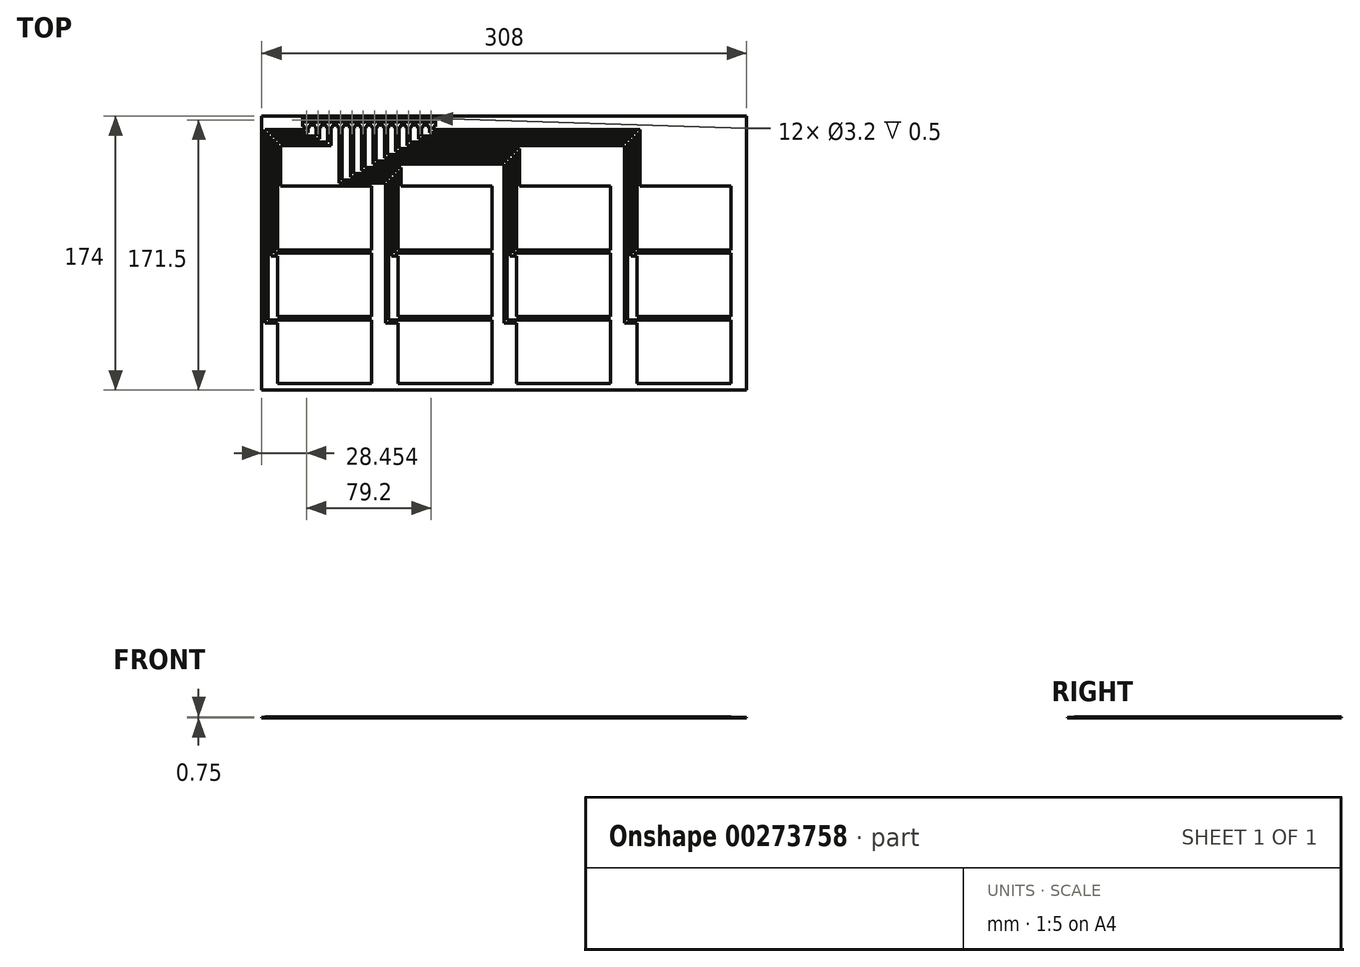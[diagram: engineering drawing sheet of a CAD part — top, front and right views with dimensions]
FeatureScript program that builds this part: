
annotation { "Feature Type Name" : "Feature", "Feature Type Description" : "" }
export const myFeature = defineFeature(function(context is Context, id is Id, definition is map)
    precondition{}
    {
        {
            var Q0;
            Q0=qCreatedBy(makeId("Top.planeOp"),FACE);
            var sketch = newSketch(context, id + "F0", { "sketchPlane" : qUnion([Q0])});
            skLineSegment(sketch, "E0.bottom", {"start": v(154, 87) * mm, "end": v(-154, 87) * mm});
            skLineSegment(sketch, "E0.top", {"start": v(154, -87) * mm, "end": v(-154, -87) * mm});
            skLineSegment(sketch, "E0.left", {"start": v(154, 87) * mm, "end": v(154, -87) * mm});
            skLineSegment(sketch, "E0.right", {"start": v(-154, 87) * mm, "end": v(-154, -87) * mm});
            skPoint(sketch, "E0.middle", {"position": v(0, 0) * mm});
            skSolve(sketch);
        }
        {
            var Q0;
            Q0=makeQuery(id+"F0.imprint","IMPRINT",FACE,{"disambiguationData":[TD([[makeQuery(id+"F0.imprint","IMPRINT",EDGE,{"derivedFrom":sQuery(id+"F0.wireOp",EDGE,"E0.bottom")}),1.0]])]});
            extrude(context, id + "F1", {"entities" : qUnion([Q0]), "depth" : .25 * mm});
        }
        {
            var Q0;
            Q0=makeQuery(id+"F1.opExtrude","CAP_FACE",FACE,{"disambiguationData":[OSD([sQuery(id+"F0.wireOp",EDGE,"E0.bottom"),sQuery(id+"F0.wireOp",EDGE,"E0.top"),sQuery(id+"F0.wireOp",EDGE,"E0.left"),sQuery(id+"F0.wireOp",EDGE,"E0.right")])],"isStart":false});
            var sketch = newSketch(context, id + "F2", { "sketchPlane" : qUnion([Q0])});
            skLineSegment(sketch, "E1", {"start": v(-85.95, 87) * mm, "end": v(-85.95, 80.4) * mm, "construction": true});
            skCircle(sketch, "E2", {"center": v(-89.55, 84.5) * mm, "radius": 1.6 * mm});
            skLineSegment(sketch, "E3", {"start": v(-89.55, 84.5) * mm, "end": v(-89.55, 80.4) * mm, "construction": true});
            skPoint(sketch, "E4", {"position": v(0, 80.62) * mm});
            skLineSegment(sketch, "E5.direction1", {"start": v(-89.55, 84.5) * mm, "end": v(-82.35, 84.5) * mm, "construction": true});
            skLineSegment(sketch, "E6", {"start": v(-86.95, 87) * mm, "end": v(-86.95, 80.4) * mm});
            skLineSegment(sketch, "E7.MirrorCS", {"start": v(-92.15, 87) * mm, "end": v(-92.15, 80.4) * mm});
            skLineSegment(sketch, "E8.trimOffspring", {"start": v(-92.15, 80.4) * mm, "end": v(-86.95, 80.4) * mm});
            skLineSegment(sketch, "E9.trimOffspring", {"start": v(-92.15, 87) * mm, "end": v(-86.95, 87) * mm});
            skCircle(sketch, "E10.1.0.0", {"center": v(-96.75, 84.5) * mm, "radius": 1.6 * mm});
            skLineSegment(sketch, "E10.1.0.1", {"start": v(-99.35, 87) * mm, "end": v(-99.35, 80.4) * mm});
            skLineSegment(sketch, "E10.1.0.2", {"start": v(-99.35, 87) * mm, "end": v(-94.15, 87) * mm});
            skLineSegment(sketch, "E10.1.0.3", {"start": v(-94.15, 87) * mm, "end": v(-94.15, 80.4) * mm});
            skLineSegment(sketch, "E10.1.0.4", {"start": v(-99.35, 80.4) * mm, "end": v(-94.15, 80.4) * mm});
            skCircle(sketch, "E10.2.0.0", {"center": v(-103.95, 84.5) * mm, "radius": 1.6 * mm});
            skLineSegment(sketch, "E10.2.0.1", {"start": v(-106.55, 87) * mm, "end": v(-106.55, 80.4) * mm});
            skLineSegment(sketch, "E10.2.0.2", {"start": v(-106.55, 87) * mm, "end": v(-101.35, 87) * mm});
            skLineSegment(sketch, "E10.2.0.3", {"start": v(-101.35, 87) * mm, "end": v(-101.35, 80.4) * mm});
            skLineSegment(sketch, "E10.2.0.4", {"start": v(-106.55, 80.4) * mm, "end": v(-101.35, 80.4) * mm});
            skCircle(sketch, "E10.3.0.0", {"center": v(-111.15, 84.5) * mm, "radius": 1.6 * mm});
            skLineSegment(sketch, "E10.3.0.1", {"start": v(-113.75, 87) * mm, "end": v(-113.75, 80.4) * mm});
            skLineSegment(sketch, "E10.3.0.2", {"start": v(-113.75, 87) * mm, "end": v(-108.55, 87) * mm});
            skLineSegment(sketch, "E10.3.0.3", {"start": v(-108.55, 87) * mm, "end": v(-108.55, 80.4) * mm});
            skLineSegment(sketch, "E10.3.0.4", {"start": v(-113.75, 80.4) * mm, "end": v(-108.55, 80.4) * mm});
            skCircle(sketch, "E10.4.0.0", {"center": v(-118.35, 84.5) * mm, "radius": 1.6 * mm});
            skLineSegment(sketch, "E10.4.0.1", {"start": v(-120.95, 87) * mm, "end": v(-120.95, 80.4) * mm});
            skLineSegment(sketch, "E10.4.0.2", {"start": v(-120.95, 87) * mm, "end": v(-115.75, 87) * mm});
            skLineSegment(sketch, "E10.4.0.3", {"start": v(-115.75, 87) * mm, "end": v(-115.75, 80.4) * mm});
            skLineSegment(sketch, "E10.4.0.4", {"start": v(-120.95, 80.4) * mm, "end": v(-115.75, 80.4) * mm});
            skCircle(sketch, "E10.5.0.0", {"center": v(-125.55, 84.5) * mm, "radius": 1.6 * mm});
            skLineSegment(sketch, "E10.5.0.1", {"start": v(-128.15, 87) * mm, "end": v(-128.15, 80.4) * mm});
            skLineSegment(sketch, "E10.5.0.2", {"start": v(-128.15, 87) * mm, "end": v(-122.95, 87) * mm});
            skLineSegment(sketch, "E10.5.0.3", {"start": v(-122.95, 87) * mm, "end": v(-122.95, 80.4) * mm});
            skLineSegment(sketch, "E10.5.0.4", {"start": v(-128.15, 80.4) * mm, "end": v(-122.95, 80.4) * mm});
            skLineSegment(sketch, "E10.direction1", {"start": v(-89.55, 84.5) * mm, "end": v(-96.75, 84.5) * mm, "construction": true});
            skCircle(sketch, "E11.MirrorC", {"center": v(-82.35, 84.5) * mm, "radius": 1.6 * mm});
            skLineSegment(sketch, "E12.MirrorCS", {"start": v(-79.75, 80.4) * mm, "end": v(-84.95, 80.4) * mm});
            skLineSegment(sketch, "E13.MirrorCS", {"start": v(-84.95, 87) * mm, "end": v(-84.95, 80.4) * mm});
            skLineSegment(sketch, "E14.MirrorCS", {"start": v(-79.75, 87) * mm, "end": v(-84.95, 87) * mm});
            skLineSegment(sketch, "E15.MirrorCS", {"start": v(-79.75, 87) * mm, "end": v(-79.75, 80.4) * mm});
            skLineSegment(sketch, "E16.MirrorCS", {"start": v(-77.75, 87) * mm, "end": v(-77.75, 80.4) * mm});
            skCircle(sketch, "E17.MirrorC", {"center": v(-75.15, 84.5) * mm, "radius": 1.6 * mm});
            skLineSegment(sketch, "E18.MirrorCS", {"start": v(-72.55, 87) * mm, "end": v(-77.75, 87) * mm});
            skLineSegment(sketch, "E19.MirrorCS", {"start": v(-72.55, 87) * mm, "end": v(-72.55, 80.4) * mm});
            skLineSegment(sketch, "E20.MirrorCS", {"start": v(-70.55, 87) * mm, "end": v(-70.55, 80.4) * mm});
            skCircle(sketch, "E21.MirrorC", {"center": v(-67.95, 84.5) * mm, "radius": 1.6 * mm});
            skLineSegment(sketch, "E22.MirrorCS", {"start": v(-65.35, 87) * mm, "end": v(-65.35, 80.4) * mm});
            skLineSegment(sketch, "E23.MirrorCS", {"start": v(-65.35, 87) * mm, "end": v(-70.55, 87) * mm});
            skLineSegment(sketch, "E24.MirrorCS", {"start": v(-63.35, 87) * mm, "end": v(-63.35, 80.4) * mm});
            skLineSegment(sketch, "E25.MirrorCS", {"start": v(-58.15, 87) * mm, "end": v(-63.35, 87) * mm});
            skCircle(sketch, "E26.MirrorC", {"center": v(-60.75, 84.5) * mm, "radius": 1.6 * mm});
            skLineSegment(sketch, "E27.MirrorCS", {"start": v(-58.15, 87) * mm, "end": v(-58.15, 80.4) * mm});
            skLineSegment(sketch, "E28.MirrorCS", {"start": v(-58.15, 80.4) * mm, "end": v(-63.35, 80.4) * mm});
            skLineSegment(sketch, "E29.MirrorCS", {"start": v(-56.15, 87) * mm, "end": v(-56.15, 80.4) * mm});
            skLineSegment(sketch, "E30.MirrorCS", {"start": v(-50.95, 87) * mm, "end": v(-56.15, 87) * mm});
            skLineSegment(sketch, "E31.MirrorCS", {"start": v(-50.95, 87) * mm, "end": v(-50.95, 80.4) * mm});
            skCircle(sketch, "E32.MirrorC", {"center": v(-53.55, 84.5) * mm, "radius": 1.6 * mm});
            skLineSegment(sketch, "E33.MirrorCS", {"start": v(-48.95, 87) * mm, "end": v(-48.95, 80.4) * mm});
            skCircle(sketch, "E34.MirrorC", {"center": v(-46.35, 84.5) * mm, "radius": 1.6 * mm});
            skLineSegment(sketch, "E35.MirrorCS", {"start": v(-43.75, 87) * mm, "end": v(-48.95, 87) * mm});
            skLineSegment(sketch, "E36.MirrorCS", {"start": v(-43.75, 87) * mm, "end": v(-43.75, 80.4) * mm});
            skLineSegment(sketch, "E37.top", {"start": v(-84.36, 0) * mm, "end": v(-144, 0) * mm});
            skLineSegment(sketch, "E37.left", {"start": v(-84.36, 42.4) * mm, "end": v(-84.36, 2) * mm});
            skLineSegment(sketch, "E38", {"start": v(0, 87) * mm, "end": v(0, -87) * mm, "construction": true});
            skLineSegment(sketch, "E39.bottom", {"start": v(-67.44, 42.4) * mm, "end": v(-7.8, 42.4) * mm});
            skLineSegment(sketch, "E39.top", {"start": v(-67.44, 2) * mm, "end": v(-7.8, 2) * mm});
            skLineSegment(sketch, "E39.left", {"start": v(-67.44, 42.4) * mm, "end": v(-67.44, 2) * mm});
            skLineSegment(sketch, "E39.right", {"start": v(-7.8, 42.4) * mm, "end": v(-7.8, 2) * mm});
            skLineSegment(sketch, "E40.bottom", {"start": v(-144, 2) * mm, "end": v(-84.36, 2) * mm});
            skLineSegment(sketch, "E40.left", {"start": v(-144, 0) * mm, "end": v(-144, -40.4) * mm});
            skLineSegment(sketch, "E41.left", {"start": v(-144, -42.4) * mm, "end": v(-144, -82.8) * mm});
            skLineSegment(sketch, "E41.right", {"start": v(-84.36, -42.4) * mm, "end": v(-84.36, -82.8) * mm});
            skLineSegment(sketch, "E42.bottom", {"start": v(-67.44, 0) * mm, "end": v(-7.8, 0) * mm});
            skLineSegment(sketch, "E42.top", {"start": v(-67.44, -40.4) * mm, "end": v(-7.8, -40.4) * mm});
            skLineSegment(sketch, "E42.left", {"start": v(-67.44, 0) * mm, "end": v(-67.44, -40.4) * mm});
            skLineSegment(sketch, "E42.right", {"start": v(-7.8, 0) * mm, "end": v(-7.8, -40.4) * mm});
            skLineSegment(sketch, "E43.bottom", {"start": v(-67.44, -42.4) * mm, "end": v(-7.8, -42.4) * mm});
            skLineSegment(sketch, "E43.top", {"start": v(-67.44, -82.8) * mm, "end": v(-7.8, -82.8) * mm});
            skLineSegment(sketch, "E43.left", {"start": v(-67.44, -42.4) * mm, "end": v(-67.44, -82.8) * mm});
            skLineSegment(sketch, "E43.right", {"start": v(-7.8, -42.4) * mm, "end": v(-7.8, -82.8) * mm});
            skLineSegment(sketch, "E44", {"start": v(-144, 87) * mm, "end": v(-154, 87) * mm, "construction": true});
            skLineSegment(sketch, "E45", {"start": v(-36.86, -77) * mm, "end": v(-36.86, -87) * mm, "construction": true});
            skLineSegment(sketch, "E46", {"start": v(-144, -40.4) * mm, "end": v(-144, -42.4) * mm, "construction": true});
            skLineSegment(sketch, "E47", {"start": v(-67.44, 2) * mm, "end": v(-67.44, 0) * mm, "construction": true});
            skLineSegment(sketch, "E48", {"start": v(-67.44, -40.4) * mm, "end": v(-67.44, -42.4) * mm, "construction": true});
            skLineSegment(sketch, "E49", {"start": v(-84.36, 0) * mm, "end": v(-84.36, -40.4) * mm});
            skLineSegment(sketch, "E50", {"start": v(-84.36, -40.4) * mm, "end": v(-144, -40.4) * mm});
            skLineSegment(sketch, "E51", {"start": v(-144, -42.4) * mm, "end": v(-84.36, -42.4) * mm});
            skLineSegment(sketch, "E52", {"start": v(-84.36, 42.4) * mm, "end": v(-67.44, 42.4) * mm, "construction": true});
            skLineSegment(sketch, "E53", {"start": v(-124.55, 80.4) * mm, "end": v(-124.55, 76.4) * mm});
            skLineSegment(sketch, "E54", {"start": v(-124.55, 76.4) * mm, "end": v(-150, 76.4) * mm});
            skLineSegment(sketch, "E55", {"start": v(-150, 76.4) * mm, "end": v(-150, -42.4) * mm});
            skPoint(sketch, "E56", {"position": v(-125.55, 80.4) * mm});
            skPoint(sketch, "E57", {"position": v(-118.35, 80.4) * mm});
            skPoint(sketch, "E58", {"position": v(-111.15, 80.4) * mm});
            skLineSegment(sketch, "E59", {"start": v(-117.35, 80.4) * mm, "end": v(-117.35, 72.4) * mm});
            skLineSegment(sketch, "E60", {"start": v(-117.35, 72.4) * mm, "end": v(-146, 72.4) * mm});
            skLineSegment(sketch, "E61", {"start": v(-146, 72.4) * mm, "end": v(-146, 0) * mm});
            skLineSegment(sketch, "E62", {"start": v(-110.15, 80.4) * mm, "end": v(-110.15, 68.4) * mm});
            skLineSegment(sketch, "E63", {"start": v(-146, 0) * mm, "end": v(-144, 0) * mm});
            skLineSegment(sketch, "E64", {"start": v(-144, -42.4) * mm, "end": v(-150, -42.4) * mm});
            skLineSegment(sketch, "E65.0", {"start": v(-148, -2) * mm, "end": v(-144, -2) * mm});
            skLineSegment(sketch, "E65.1", {"start": v(-148, 74.4) * mm, "end": v(-148, -2) * mm});
            skLineSegment(sketch, "E65.2", {"start": v(-119.35, 74.4) * mm, "end": v(-148, 74.4) * mm});
            skLineSegment(sketch, "E65.3", {"start": v(-119.35, 80.4) * mm, "end": v(-119.35, 74.4) * mm});
            skLineSegment(sketch, "E66.0", {"start": v(-144, -44.4) * mm, "end": v(-152, -44.4) * mm});
            skLineSegment(sketch, "E66.1", {"start": v(-152, 78.4) * mm, "end": v(-152, -44.4) * mm});
            skLineSegment(sketch, "E66.2", {"start": v(-126.55, 78.4) * mm, "end": v(-152, 78.4) * mm});
            skLineSegment(sketch, "E66.3", {"start": v(-126.55, 80.4) * mm, "end": v(-126.55, 78.4) * mm});
            skPoint(sketch, "E67", {"position": v(-103.95, 80.4) * mm});
            skPoint(sketch, "E68", {"position": v(-96.75, 80.4) * mm});
            skPoint(sketch, "E69", {"position": v(-82.35, 80.4) * mm});
            skPoint(sketch, "E70", {"position": v(-75.15, 80.4) * mm});
            skLineSegment(sketch, "E71", {"start": v(-102.95, 80.4) * mm, "end": v(-102.95, 46.4) * mm});
            skLineSegment(sketch, "E72", {"start": v(-102.95, 46.4) * mm, "end": v(-73.44, 46.4) * mm});
            skLineSegment(sketch, "E73", {"start": v(-73.44, 46.4) * mm, "end": v(-73.44, -42.4) * mm});
            skLineSegment(sketch, "E74", {"start": v(-73.44, -42.4) * mm, "end": v(-67.44, -42.4) * mm});
            skLineSegment(sketch, "E75", {"start": v(-95.75, 80.4) * mm, "end": v(-95.75, 50.4) * mm});
            skLineSegment(sketch, "E76", {"start": v(-95.75, 50.4) * mm, "end": v(-69.44, 50.4) * mm});
            skLineSegment(sketch, "E77", {"start": v(-69.44, 50.4) * mm, "end": v(-69.44, 0) * mm});
            skLineSegment(sketch, "E78", {"start": v(-69.44, 0) * mm, "end": v(-67.44, 0) * mm});
            skLineSegment(sketch, "E79.0", {"start": v(-75.44, -44.4) * mm, "end": v(-67.44, -44.4) * mm});
            skLineSegment(sketch, "E79.1", {"start": v(-75.44, 44.4) * mm, "end": v(-75.44, -44.4) * mm});
            skLineSegment(sketch, "E79.2", {"start": v(-104.95, 44.4) * mm, "end": v(-75.44, 44.4) * mm});
            skLineSegment(sketch, "E79.3", {"start": v(-104.95, 80.4) * mm, "end": v(-104.95, 44.4) * mm});
            skLineSegment(sketch, "E80.0", {"start": v(-71.44, -2) * mm, "end": v(-67.44, -2) * mm});
            skLineSegment(sketch, "E80.1", {"start": v(-71.44, 48.4) * mm, "end": v(-71.44, -2) * mm});
            skLineSegment(sketch, "E80.2", {"start": v(-97.75, 48.4) * mm, "end": v(-71.44, 48.4) * mm});
            skLineSegment(sketch, "E80.3", {"start": v(-97.75, 80.4) * mm, "end": v(-97.75, 48.4) * mm});
            skLineSegment(sketch, "E81", {"start": v(-84.36, -42.4) * mm, "end": v(-73.44, -42.4) * mm, "construction": true});
            skLineSegment(sketch, "E82", {"start": v(-84.36, 0) * mm, "end": v(-69.44, 0) * mm, "construction": true});
            skLineSegment(sketch, "E83", {"start": v(-88.55, 80.4) * mm, "end": v(-88.55, 54.4) * mm});
            skLineSegment(sketch, "E84", {"start": v(-88.55, 54.4) * mm, "end": v(-65.44, 54.4) * mm});
            skLineSegment(sketch, "E85", {"start": v(-65.44, 54.4) * mm, "end": v(-65.44, 42.4) * mm});
            skLineSegment(sketch, "E86", {"start": v(-81.35, 80.4) * mm, "end": v(-81.35, 58.4) * mm});
            skLineSegment(sketch, "E87", {"start": v(-144, 42.4) * mm, "end": v(-144, 2) * mm});
            skLineSegment(sketch, "E88", {"start": v(-144, 2) * mm, "end": v(-144, 0) * mm, "construction": true});
            skLineSegment(sketch, "E89.MirrorCS", {"start": v(7.8, 42.4) * mm, "end": v(7.8, 2) * mm});
            skLineSegment(sketch, "E90.MirrorCS", {"start": v(67.44, 42.4) * mm, "end": v(7.8, 42.4) * mm});
            skLineSegment(sketch, "E91.MirrorCS", {"start": v(67.44, 42.4) * mm, "end": v(67.44, 2) * mm});
            skLineSegment(sketch, "E92.MirrorCS", {"start": v(67.44, 2) * mm, "end": v(7.8, 2) * mm});
            skLineSegment(sketch, "E93.MirrorCS", {"start": v(84.36, 42.4) * mm, "end": v(84.36, 2) * mm});
            skLineSegment(sketch, "E94.MirrorCS", {"start": v(84.36, 42.4) * mm, "end": v(144, 42.4) * mm});
            skLineSegment(sketch, "E95.MirrorCS", {"start": v(144, 42.4) * mm, "end": v(144, 2) * mm});
            skLineSegment(sketch, "E96.MirrorCS", {"start": v(144, 2) * mm, "end": v(84.36, 2) * mm});
            skLineSegment(sketch, "E97.MirrorCS", {"start": v(84.36, 0) * mm, "end": v(144, 0) * mm});
            skLineSegment(sketch, "E98.MirrorCS", {"start": v(144, 0) * mm, "end": v(144, -40.4) * mm});
            skLineSegment(sketch, "E99.MirrorCS", {"start": v(84.36, 0) * mm, "end": v(84.36, -40.4) * mm});
            skLineSegment(sketch, "E100.MirrorCS", {"start": v(144, -42.4) * mm, "end": v(84.36, -42.4) * mm});
            skLineSegment(sketch, "E101.MirrorCS", {"start": v(84.36, -42.4) * mm, "end": v(84.36, -82.8) * mm});
            skLineSegment(sketch, "E102.MirrorCS", {"start": v(67.44, -42.4) * mm, "end": v(67.44, -82.8) * mm});
            skLineSegment(sketch, "E103.MirrorCS", {"start": v(7.8, -42.4) * mm, "end": v(7.8, -82.8) * mm});
            skLineSegment(sketch, "E104.MirrorCS", {"start": v(67.44, -42.4) * mm, "end": v(7.8, -42.4) * mm});
            skLineSegment(sketch, "E105.MirrorCS", {"start": v(67.44, -40.4) * mm, "end": v(7.8, -40.4) * mm});
            skLineSegment(sketch, "E106.MirrorCS", {"start": v(7.8, 0) * mm, "end": v(7.8, -40.4) * mm});
            skLineSegment(sketch, "E107.MirrorCS", {"start": v(67.44, 0) * mm, "end": v(67.44, -40.4) * mm});
            skLineSegment(sketch, "E108.MirrorCS", {"start": v(67.44, 0) * mm, "end": v(7.8, 0) * mm});
            skLineSegment(sketch, "E109.MirrorCS", {"start": v(84.36, -40.4) * mm, "end": v(144, -40.4) * mm});
            skLineSegment(sketch, "E110", {"start": v(7.8, -82.8) * mm, "end": v(67.44, -82.8) * mm});
            skLineSegment(sketch, "E111", {"start": v(1.8, 58.4) * mm, "end": v(1.8, -42.4) * mm});
            skLineSegment(sketch, "E112", {"start": v(-81.35, 58.4) * mm, "end": v(1.8, 58.4) * mm});
            skLineSegment(sketch, "E113", {"start": v(7.8, -42.4) * mm, "end": v(1.8, -42.4) * mm});
            skLineSegment(sketch, "E114.0", {"start": v(-67.44, 52.4) * mm, "end": v(-67.44, 42.4) * mm});
            skLineSegment(sketch, "E114.1", {"start": v(-90.55, 52.4) * mm, "end": v(-67.44, 52.4) * mm});
            skLineSegment(sketch, "E114.2", {"start": v(-90.55, 80.4) * mm, "end": v(-90.55, 52.4) * mm});
            skLineSegment(sketch, "E115.0", {"start": v(7.8, -44.4) * mm, "end": v(-0.2, -44.4) * mm});
            skLineSegment(sketch, "E115.1", {"start": v(-0.2, 56.4) * mm, "end": v(-0.2, -44.4) * mm});
            skLineSegment(sketch, "E115.2", {"start": v(-83.35, 56.4) * mm, "end": v(-0.2, 56.4) * mm});
            skLineSegment(sketch, "E115.3", {"start": v(-83.35, 80.4) * mm, "end": v(-83.35, 56.4) * mm});
            skLineSegment(sketch, "E116", {"start": v(-74.15, 80.4) * mm, "end": v(-74.15, 62.4) * mm});
            skLineSegment(sketch, "E117", {"start": v(-74.15, 62.4) * mm, "end": v(5.8, 62.4) * mm});
            skLineSegment(sketch, "E118", {"start": v(5.8, 62.4) * mm, "end": v(5.8, 0) * mm});
            skLineSegment(sketch, "E119", {"start": v(5.8, 0) * mm, "end": v(7.8, 0) * mm});
            skLineSegment(sketch, "E120.0", {"start": v(3.8, -2) * mm, "end": v(7.8, -2) * mm});
            skLineSegment(sketch, "E120.1", {"start": v(3.8, 60.4) * mm, "end": v(3.8, -2) * mm});
            skLineSegment(sketch, "E120.2", {"start": v(-76.15, 60.4) * mm, "end": v(3.8, 60.4) * mm});
            skLineSegment(sketch, "E120.3", {"start": v(-76.15, 80.4) * mm, "end": v(-76.15, 60.4) * mm});
            skLineSegment(sketch, "E121", {"start": v(-66.95, 80.4) * mm, "end": v(-66.95, 66.4) * mm});
            skLineSegment(sketch, "E122", {"start": v(-66.95, 66.4) * mm, "end": v(9.8, 66.4) * mm});
            skLineSegment(sketch, "E123", {"start": v(9.8, 66.4) * mm, "end": v(9.8, 42.4) * mm});
            skLineSegment(sketch, "E124.0", {"start": v(7.8, 64.4) * mm, "end": v(7.8, 42.4) * mm});
            skLineSegment(sketch, "E124.1", {"start": v(-68.95, 64.4) * mm, "end": v(7.8, 64.4) * mm});
            skLineSegment(sketch, "E124.2", {"start": v(-68.95, 80.4) * mm, "end": v(-68.95, 64.4) * mm});
            skLineSegment(sketch, "E125", {"start": v(-59.75, 80.4) * mm, "end": v(-59.75, 70.4) * mm});
            skLineSegment(sketch, "E126", {"start": v(-59.75, 70.4) * mm, "end": v(78.36, 70.4) * mm});
            skLineSegment(sketch, "E127", {"start": v(78.36, 70.4) * mm, "end": v(78.36, -42.4) * mm});
            skLineSegment(sketch, "E128", {"start": v(78.36, -42.4) * mm, "end": v(84.36, -42.4) * mm});
            skLineSegment(sketch, "E129.2", {"start": v(-61.75, 68.4) * mm, "end": v(76.36, 68.4) * mm});
            skLineSegment(sketch, "E129.3", {"start": v(-61.75, 80.4) * mm, "end": v(-61.75, 68.4) * mm});
            skLineSegment(sketch, "E130", {"start": v(82.36, 74.4) * mm, "end": v(82.36, 0) * mm});
            skLineSegment(sketch, "E131", {"start": v(82.36, 0) * mm, "end": v(84.36, 0) * mm});
            skLineSegment(sketch, "E132.0", {"start": v(80.36, -2) * mm, "end": v(84.36, -2) * mm});
            skLineSegment(sketch, "E132.1", {"start": v(80.36, 72.4) * mm, "end": v(80.36, -2) * mm});
            skLineSegment(sketch, "E132.2", {"start": v(-54.55, 72.4) * mm, "end": v(80.36, 72.4) * mm});
            skLineSegment(sketch, "E132.3", {"start": v(-54.55, 80.4) * mm, "end": v(-54.55, 72.4) * mm});
            skLineSegment(sketch, "E133", {"start": v(-45.35, 80.4) * mm, "end": v(-45.35, 78.4) * mm});
            skLineSegment(sketch, "E134", {"start": v(-45.35, 78.4) * mm, "end": v(86.36, 78.4) * mm});
            skLineSegment(sketch, "E135", {"start": v(86.36, 78.4) * mm, "end": v(86.36, 42.4) * mm});
            skLineSegment(sketch, "E136.0", {"start": v(84.36, 76.4) * mm, "end": v(84.36, 42.4) * mm});
            skLineSegment(sketch, "E136.1", {"start": v(-47.35, 76.4) * mm, "end": v(84.36, 76.4) * mm});
            skLineSegment(sketch, "E137", {"start": v(-144, 42.4) * mm, "end": v(-84.36, 42.4) * mm});
            skLineSegment(sketch, "E138", {"start": v(-112.15, 80.4) * mm, "end": v(-112.15, 70.4) * mm});
            skLineSegment(sketch, "E139", {"start": v(-112.15, 70.4) * mm, "end": v(-144, 70.4) * mm});
            skLineSegment(sketch, "E140", {"start": v(-144, 70.4) * mm, "end": v(-144, 42.4) * mm});
            skLineSegment(sketch, "E141.0", {"start": v(-142, 68.4) * mm, "end": v(-142, 42.4) * mm});
            skLineSegment(sketch, "E141.1", {"start": v(-110.15, 68.4) * mm, "end": v(-142, 68.4) * mm});
            skLineSegment(sketch, "E142", {"start": v(76.36, 68.4) * mm, "end": v(76.36, -44.4) * mm});
            skLineSegment(sketch, "E143", {"start": v(76.36, -44.4) * mm, "end": v(84.36, -44.4) * mm});
            skLineSegment(sketch, "E144", {"start": v(-56.15, 80.4) * mm, "end": v(-50.95, 80.4) * mm});
            skPoint(sketch, "E145", {"position": v(-53.55, 80.4) * mm});
            skLineSegment(sketch, "E146", {"start": v(-70.55, 80.4) * mm, "end": v(-65.35, 80.4) * mm});
            skPoint(sketch, "E147", {"position": v(-67.95, 80.4) * mm});
            skLineSegment(sketch, "E148", {"start": v(-67.95, 84.5) * mm, "end": v(-67.95, 80.4) * mm, "construction": true});
            skLineSegment(sketch, "E149", {"start": v(-60.75, 84.5) * mm, "end": v(-60.75, 80.4) * mm, "construction": true});
            skLineSegment(sketch, "E150", {"start": v(-52.55, 80.4) * mm, "end": v(-52.55, 74.4) * mm});
            skLineSegment(sketch, "E151", {"start": v(-52.55, 74.4) * mm, "end": v(82.36, 74.4) * mm});
            skLineSegment(sketch, "E152", {"start": v(-47.35, 80.4) * mm, "end": v(-47.35, 76.4) * mm});
            skLineSegment(sketch, "E153", {"start": v(-77.75, 80.4) * mm, "end": v(-72.55, 80.4) * mm});
            skLineSegment(sketch, "E154", {"start": v(-48.95, 80.4) * mm, "end": v(-43.75, 80.4) * mm});
            skLineSegment(sketch, "E155", {"start": v(-46.35, 84.5) * mm, "end": v(-46.35, 80.4) * mm, "construction": true});
            skLineSegment(sketch, "E156", {"start": v(-144, -82.8) * mm, "end": v(-84.36, -82.8) * mm});
            skLineSegment(sketch, "E157", {"start": v(84.36, -82.8) * mm, "end": v(144.1, -82.8) * mm});
            skPoint(sketch, "E158.MirrorCS.start.orphan", {"position": v(144, -42.4) * mm});
            skLineSegment(sketch, "E159", {"start": v(144, -42.4) * mm, "end": v(144.1, -82.8) * mm});
            skSolve(sketch);
        }
        {
            var Q0;
            Q0 = qSketchRegion(id + "F2", true);
            extrude(context, id + "F3", {"entities" : qUnion([Q0]), "operationType" : NewBodyOperationType.ADD, "depth" : .5 * mm});
        }
    });
